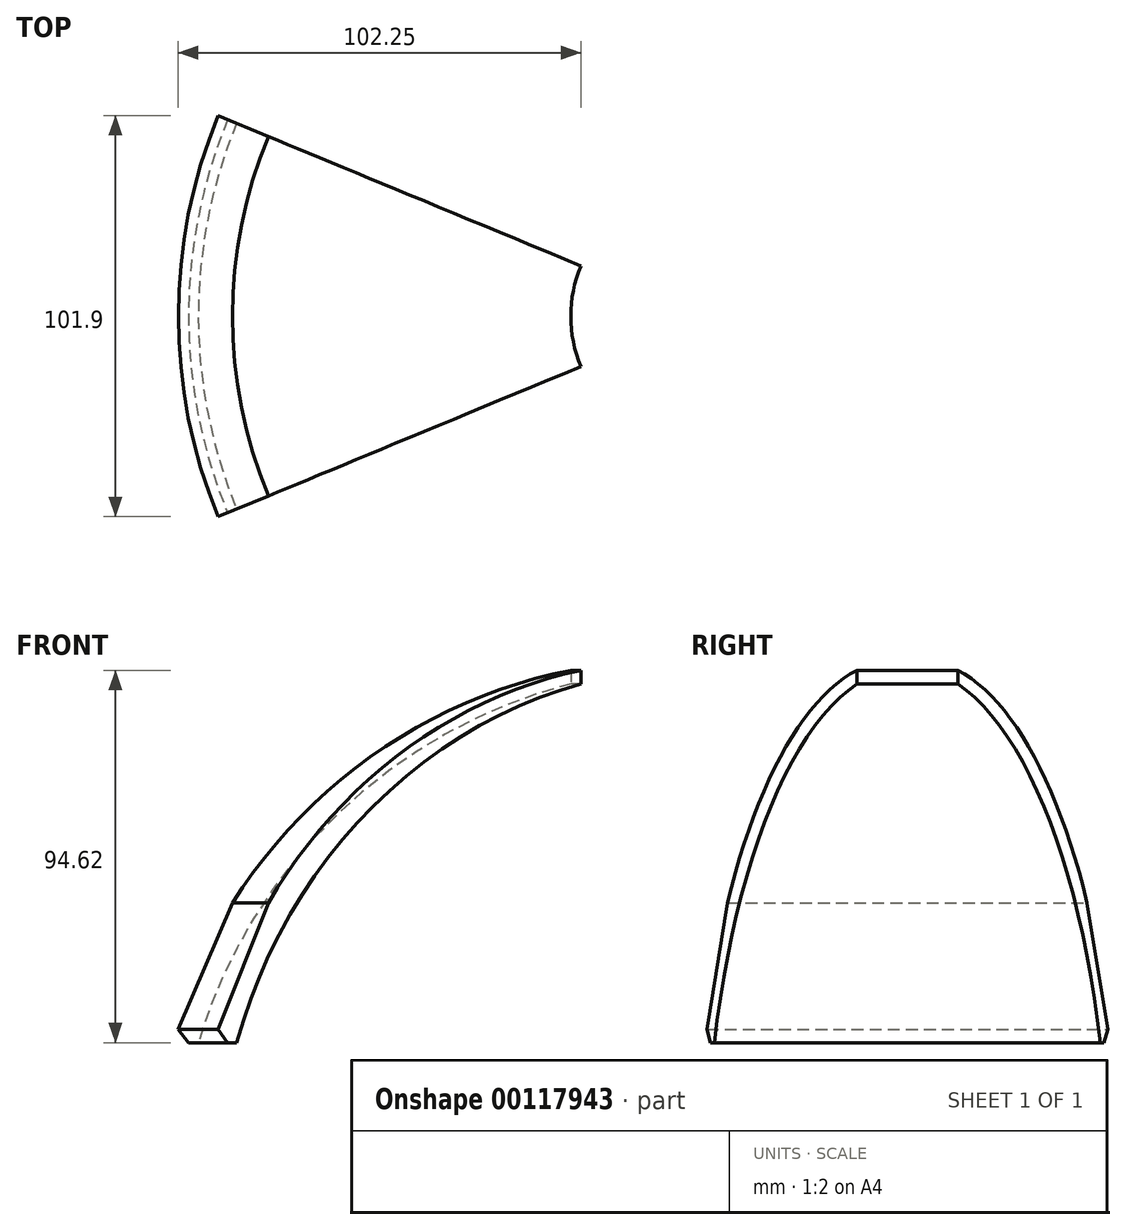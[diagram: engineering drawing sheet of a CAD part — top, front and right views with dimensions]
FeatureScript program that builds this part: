
annotation { "Feature Type Name" : "Feature", "Feature Type Description" : "" }
export const myFeature = defineFeature(function(context is Context, id is Id, definition is map)
    precondition{}
    {
        {
            var Q0;
            Q0=qCreatedBy(makeId("Front.planeOp"),FACE);
            var sketch = newSketch(context, id + "F0", { "sketchPlane" : qUnion([Q0])});
            skCircle(sketch, "E0", {"center": v(0, 0) * mm, "radius": 137 * mm});
            skLineSegment(sketch, "E1", {"start": v(0, 0) * mm, "end": v(59.98, 0) * mm, "construction": true});
            skLineSegment(sketch, "E2", {"start": v(0, 32) * mm, "end": v(61, 32) * mm, "construction": true});
            skLineSegment(sketch, "E3", {"start": v(0, 74.5) * mm, "end": v(61, 74.5) * mm, "construction": true});
            skLineSegment(sketch, "E4", {"start": v(-114.97, 74.5) * mm, "end": v(114.97, 74.5) * mm});
            skLineSegment(sketch, "E5", {"start": v(-133.21, 32) * mm, "end": v(133.21, 32) * mm});
            skLineSegment(sketch, "E6", {"start": v(114.97, 74.5) * mm, "end": v(133.21, 32) * mm});
            skLineSegment(sketch, "E7", {"start": v(-114.97, 74.5) * mm, "end": v(-133.21, 32) * mm});
            skLineSegment(sketch, "E8", {"start": v(-129.2, 32) * mm, "end": v(-110.96, 74.5) * mm});
            skCircle(sketch, "E9", {"center": v(0, 0) * mm, "radius": 133.65 * mm});
            skLineSegment(sketch, "E10", {"start": v(0, 133.65) * mm, "end": v(0, 137) * mm});
            skLineSegment(sketch, "E11", {"start": v(-129.2, 32) * mm, "end": v(-133.21, 32) * mm});
            skLineSegment(sketch, "E12", {"start": v(-130.53, 38.24) * mm, "end": v(-133.13, 41.63) * mm});
            skLineSegment(sketch, "E13", {"start": v(-133.13, 41.63) * mm, "end": v(-119.35, 73.73) * mm});
            skLineSegment(sketch, "E14", {"start": v(-121.02, 69.84) * mm, "end": v(-121.02, 129.84) * mm, "construction": true});
            skLineSegment(sketch, "E15", {"start": v(-121.02, 129.84) * mm, "end": v(-43.71, 129.84) * mm, "construction": true});
            skArc(sketch, "E16", {"start": v(-33.42, 132.86) * mm, "mid": v(-82.47, 112.14) * mm, "end": v(-119.35, 73.73) * mm});
            skLineSegment(sketch, "E17", {"start": v(-33.42, 132.86) * mm, "end": v(-33.42, 129.4) * mm});
            skLineSegment(sketch, "E18", {"start": v(-130.53, 38.24) * mm, "end": v(-128.06, 38.24) * mm});
            skSolve(sketch);
        }
        {
            var Q0;
            {var subQ0=sQuery(id+"F0.wireOp",EDGE,"E13");Q0=makeQuery(id+"F0.imprint","IMPRINT",FACE,{"disambiguationData":[TD([[makeQuery(id+"F0.imprint","IMPRINT",EDGE,{"derivedFrom":subQ0}),-1.0]])]});}
            var Q1;
            {var subQ1=sQuery(id+"F0.wireOp",EDGE,"E0");var subQ3=sQuery(id+"F0.wireOp",EDGE,"E12");var subQ4=makeQuery(id+"F0.imprint","INTERSECT",VERTEX,{"derivedFrom":[subQ1,subQ3]});Q1=makeQuery(id+"F0.imprint","IMPRINT",FACE,{"disambiguationData":[TD([[makeQuery(id+"F0.imprint","IMPRINT",EDGE,{"disambiguationData":[TD([[subQ4,1.0]])],"derivedFrom":subQ1}),1.0]])]});}
            var Q2;
            {var subQ5=sQuery(id+"F0.wireOp",EDGE,"E18");Q2=makeQuery(id+"F0.imprint","IMPRINT",FACE,{"disambiguationData":[TD([[makeQuery(id+"F0.imprint","IMPRINT",EDGE,{"derivedFrom":subQ5}),1.0]])]});}
            var Q3;
            {var subQ3=sQuery(id+"F0.wireOp",EDGE,"E17");Q3=makeQuery(id+"F0.imprint","IMPRINT",FACE,{"disambiguationData":[TD([[makeQuery(id+"F0.imprint","IMPRINT",EDGE,{"derivedFrom":subQ3}),-1.0]])]});}
            var Q4;
            Q4=sQuery(id+"F0.wireOp",EDGE,"E10");
            revolve(context, id + "F1", {"entities" : qUnion([Q0, Q1, Q2, Q3]), "axis" : qUnion([Q4]), "revolveType" : RevolveType.SYMMETRIC, "angle" : 45 * degree});
        }
    });
